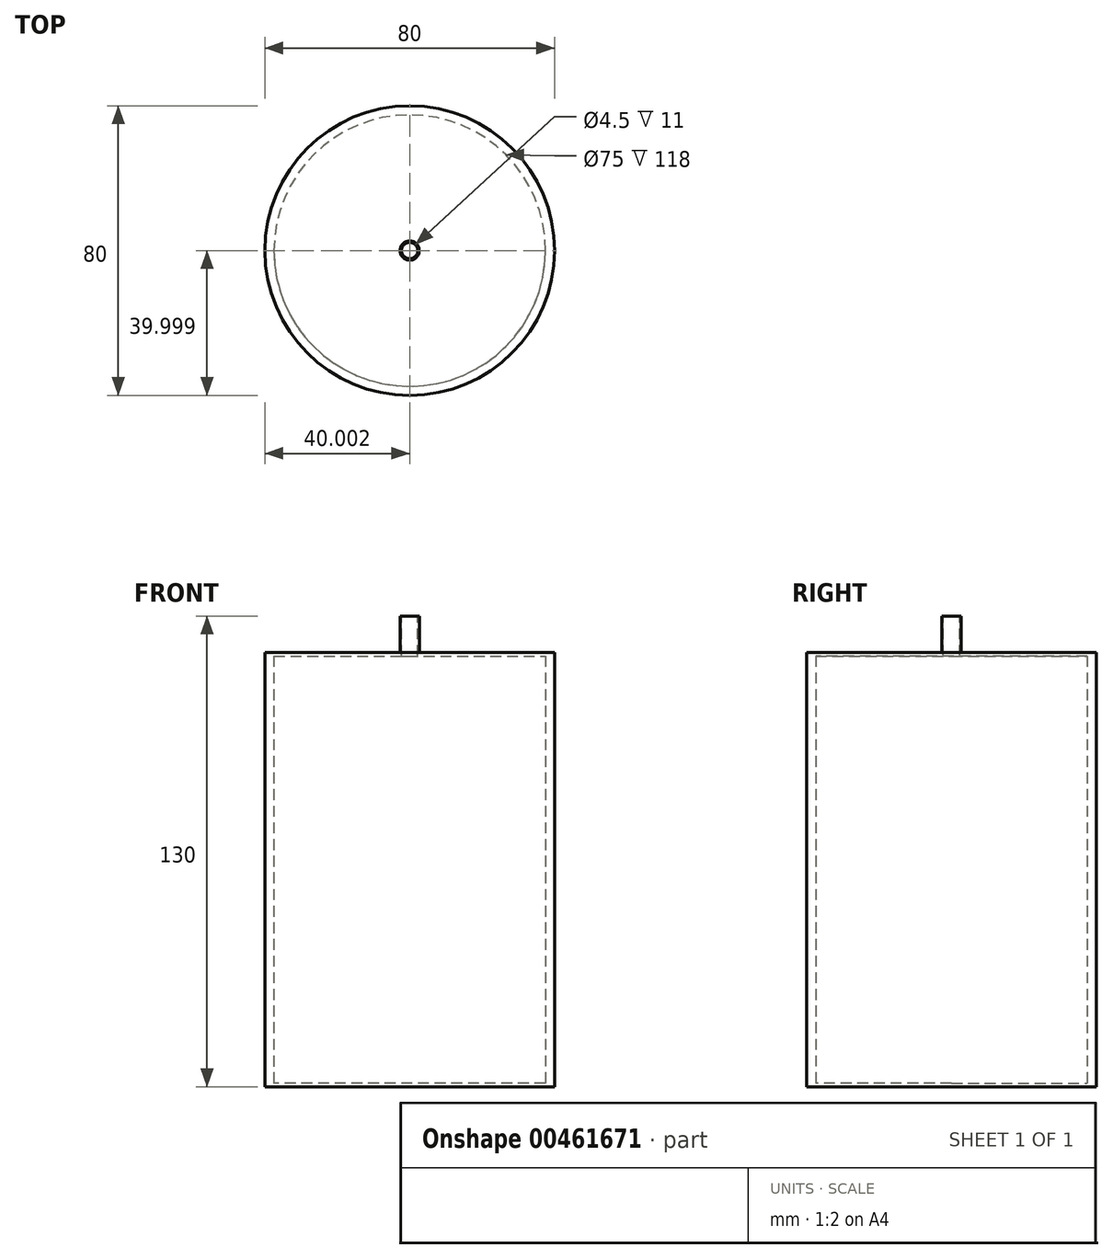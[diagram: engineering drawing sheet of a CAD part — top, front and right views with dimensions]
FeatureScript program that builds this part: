
annotation { "Feature Type Name" : "Feature", "Feature Type Description" : "" }
export const myFeature = defineFeature(function(context is Context, id is Id, definition is map)
    precondition{}
    {
        {
            var Q0;
            Q0=qCreatedBy(makeId("Top.planeOp"),FACE);
            var sketch = newSketch(context, id + "F0", { "sketchPlane" : qUnion([Q0])});
            skCircle(sketch, "E0", {"center": v(-32.72, 13.76) * mm, "radius": 40 * mm});
            skSolve(sketch);
        }
        {
            var Q0;
            Q0 = qSketchRegion(id + "F0", true);
            extrude(context, id + "F1", {"entities" : qUnion([Q0]), "depth" : 120 * mm});
        }
        {
            var Q0;
            Q0=makeQuery(id+"F1.opExtrude","CAP_FACE",FACE,{"disambiguationData":[OSD([sQuery(id+"F0.wireOp",EDGE,"E0")])],"isStart":false});
            var sketch = newSketch(context, id + "F2", { "sketchPlane" : qUnion([Q0])});
            skCircle(sketch, "E1", {"center": v(-32.72, 13.76) * mm, "radius": 2.65 * mm});
            skSolve(sketch);
        }
        {
            var Q0;
            Q0=makeQuery(id+"F2.imprint","IMPRINT",FACE,{"disambiguationData":[TD([[makeQuery(id+"F2.imprint","IMPRINT",EDGE,{"derivedFrom":sQuery(id+"F2.wireOp",EDGE,"E1")}),1.0]])]});
            extrude(context, id + "F3", {"entities" : qUnion([Q0]), "operationType" : NewBodyOperationType.ADD, "depth" : 10 * mm});
        }
        {
            var Q0;
            Q0=makeQuery(id+"F3.opExtrude","CAP_FACE",FACE,{"disambiguationData":[OSD([sQuery(id+"F2.wireOp",EDGE,"E1")])],"isStart":false});
            var sketch = newSketch(context, id + "F4", { "sketchPlane" : qUnion([Q0])});
            skCircle(sketch, "E2", {"center": v(-32.72, 13.76) * mm, "radius": 2.25 * mm});
            skSolve(sketch);
        }
        {
            var Q0;
            Q0=makeQuery(id+"F4.imprint","IMPRINT",FACE,{"disambiguationData":[TD([[makeQuery(id+"F4.imprint","IMPRINT",EDGE,{"derivedFrom":sQuery(id+"F4.wireOp",EDGE,"E2")}),1.0]])]});
            extrude(context, id + "F5", {"entities" : qUnion([Q0]), "operationType" : NewBodyOperationType.REMOVE, "oppositeDirection" : true, "depth" : 25 * mm});
        }
        {
            var Q0;
            Q0=makeQuery(id+"F1.opExtrude","CAP_FACE",FACE,{"disambiguationData":[OSD([sQuery(id+"F0.wireOp",EDGE,"E0")])],"isStart":true});
            var sketch = newSketch(context, id + "F6", { "sketchPlane" : qUnion([Q0])});
            skCircle(sketch, "E3", {"center": v(-32.72, -13.76) * mm, "radius": 37.5 * mm});
            skSolve(sketch);
        }
        {
            var Q0;
            Q0=makeQuery(id+"F6.imprint","IMPRINT",FACE,{"disambiguationData":[TD([[makeQuery(id+"F6.imprint","IMPRINT",EDGE,{"derivedFrom":sQuery(id+"F6.wireOp",EDGE,"E3")}),1.0]])]});
            extrude(context, id + "F7", {"entities" : qUnion([Q0]), "operationType" : NewBodyOperationType.REMOVE, "oppositeDirection" : true, "depth" : 119 * mm});
        }
        {
            var Q0;
            Q0=qCreatedBy(makeId("Top.planeOp"),FACE);
            var sketch = newSketch(context, id + "F8", { "sketchPlane" : qUnion([Q0])});
            skCircle(sketch, "E4", {"center": v(-32.78, 13.6) * mm, "radius": 39.7 * mm});
            skSolve(sketch);
        }
        {
            var Q0;
            Q0=makeQuery(id+"F8.imprint","IMPRINT",FACE,{"disambiguationData":[TD([[makeQuery(id+"F8.imprint","IMPRINT",EDGE,{"derivedFrom":sQuery(id+"F8.wireOp",EDGE,"E4")}),1.0]])]});
            extrude(context, id + "F9", {"entities" : qUnion([Q0]), "operationType" : NewBodyOperationType.ADD, "depth" : 1 * mm});
        }
    });
